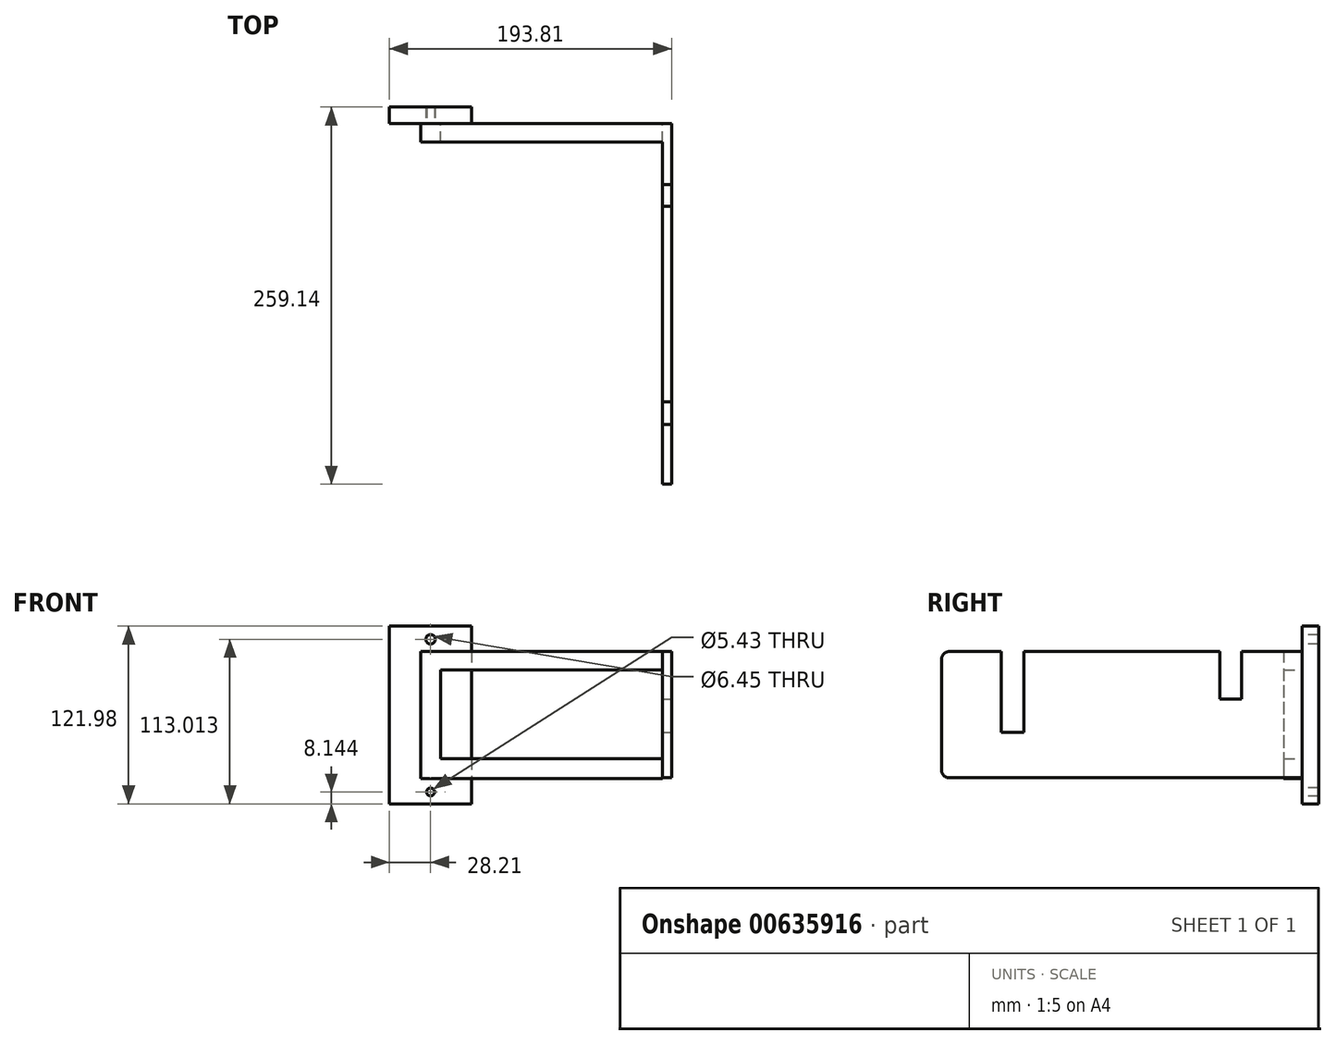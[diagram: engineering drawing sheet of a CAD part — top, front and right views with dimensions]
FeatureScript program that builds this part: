
annotation { "Feature Type Name" : "Feature", "Feature Type Description" : "" }
export const myFeature = defineFeature(function(context is Context, id is Id, definition is map)
    precondition{}
    {
        {
            var Q0;
            Q0=qCreatedBy(makeId("Front.planeOp"),FACE);
            var sketch = newSketch(context, id + "F0", { "sketchPlane" : qUnion([Q0])});
            skLineSegment(sketch, "E0.bottom", {"start": v(28.21, 61) * mm, "end": v(-28.21, 61) * mm});
            skLineSegment(sketch, "E0.top", {"start": v(28.21, -61) * mm, "end": v(-28.21, -61) * mm});
            skLineSegment(sketch, "E0.left", {"start": v(28.21, 61) * mm, "end": v(28.21, -61) * mm});
            skLineSegment(sketch, "E0.right", {"start": v(-28.21, 61) * mm, "end": v(-28.21, -61) * mm});
            skPoint(sketch, "E0.middle", {"position": v(0, 0) * mm});
            skSolve(sketch);
        }
        {
            var Q0;
            Q0=makeQuery(id+"F0.imprint","IMPRINT",FACE,{"disambiguationData":[TD([[makeQuery(id+"F0.imprint","IMPRINT",EDGE,{"derivedFrom":sQuery(id+"F0.wireOp",EDGE,"E0.bottom")}),1.0]])]});
            extrude(context, id + "F1", {"entities" : qUnion([Q0]), "depth" : 6.35 * mm, "offsetDistance" : 25.4 * mm});
        }
        {
            var Q0;
            Q0=makeQuery(id+"F1.opExtrude","CAP_FACE",FACE,{"disambiguationData":[OSD([sQuery(id+"F0.wireOp",EDGE,"E0.bottom"),sQuery(id+"F0.wireOp",EDGE,"E0.top"),sQuery(id+"F0.wireOp",EDGE,"E0.left"),sQuery(id+"F0.wireOp",EDGE,"E0.right")])],"isStart":false});
            var sketch = newSketch(context, id + "F2", { "sketchPlane" : qUnion([Q0])});
            skLineSegment(sketch, "E1.bottom", {"start": v(6.85, 43.57) * mm, "end": v(-6.85, 43.57) * mm});
            skLineSegment(sketch, "E1.top", {"start": v(6.85, -43.57) * mm, "end": v(-6.85, -43.57) * mm});
            skLineSegment(sketch, "E1.left", {"start": v(6.85, 43.57) * mm, "end": v(6.85, -43.57) * mm});
            skLineSegment(sketch, "E1.right", {"start": v(-6.85, 43.57) * mm, "end": v(-6.85, -43.57) * mm});
            skPoint(sketch, "E1.middle", {"position": v(0, 0) * mm});
            skSolve(sketch);
        }
        {
            var Q0;
            Q0 = qSketchRegion(id + "F2", true);
            extrude(context, id + "F3", {"entities" : qUnion([Q0]), "operationType" : NewBodyOperationType.ADD, "depth" : 12.7 * mm, "offsetDistance" : 25.4 * mm});
        }
        {
            var Q0;
            Q0=makeQuery(id+"F3.opExtrude","SWEPT_FACE",FACE,{"disambiguationData":[OSD([sQuery(id+"F2.wireOp",EDGE,"E1.left")])]});
            var sketch = newSketch(context, id + "F4", { "sketchPlane" : qUnion([Q0])});
            skLineSegment(sketch, "E2.bottom", {"start": v(-19.05, 43.57) * mm, "end": v(-6.35, 43.57) * mm});
            skLineSegment(sketch, "E2.top", {"start": v(-19.05, 30.9) * mm, "end": v(-6.35, 30.9) * mm});
            skLineSegment(sketch, "E2.left", {"start": v(-19.05, 43.57) * mm, "end": v(-19.05, 30.9) * mm});
            skLineSegment(sketch, "E2.right", {"start": v(-6.35, 43.57) * mm, "end": v(-6.35, 30.9) * mm});
            skSolve(sketch);
        }
        {
            var Q0;
            Q0 = qSketchRegion(id + "F4", true);
            extrude(context, id + "F5", {"entities" : qUnion([Q0]), "operationType" : NewBodyOperationType.ADD, "depth" : 152.4 * mm, "offsetDistance" : 25.4 * mm});
        }
        {
            var Q0;
            Q0=makeQuery(id+"F3.opExtrude","SWEPT_FACE",FACE,{"disambiguationData":[OSD([sQuery(id+"F2.wireOp",EDGE,"E1.left")])]});
            var sketch = newSketch(context, id + "F6", { "sketchPlane" : qUnion([Q0])});
            skLineSegment(sketch, "E3.bottom", {"start": v(-19.05, -43.57) * mm, "end": v(-6.35, -43.57) * mm});
            skLineSegment(sketch, "E3.top", {"start": v(-19.05, -30.1) * mm, "end": v(-6.35, -30.1) * mm});
            skLineSegment(sketch, "E3.left", {"start": v(-19.05, -43.57) * mm, "end": v(-19.05, -30.1) * mm});
            skLineSegment(sketch, "E3.right", {"start": v(-6.35, -43.57) * mm, "end": v(-6.35, -30.1) * mm});
            skSolve(sketch);
        }
        {
            var Q0;
            Q0 = qSketchRegion(id + "F6", true);
            extrude(context, id + "F7", {"entities" : qUnion([Q0]), "operationType" : NewBodyOperationType.ADD, "depth" : 152.4 * mm, "offsetDistance" : 25.4 * mm});
        }
        {
            var Q0;
            {var subQ0=sQuery(id+"F0.wireOp",EDGE,"E0.left");var subQ1=sQuery(id+"F0.wireOp",EDGE,"E0.bottom");var subQ2=sQuery(id+"F0.wireOp",EDGE,"E0.right");var subQ3=sQuery(id+"F0.wireOp",EDGE,"E0.top");Q0=makeQuery(id+"F7.boolean.opBoolean","SPLIT",FACE,{"disambiguationData":[TD([makeQuery(id+"F1.opExtrude","SWEPT_FACE",FACE,{"disambiguationData":[OSD([subQ1])]})])],"derivedFrom":makeQuery(id+"F1.opExtrude","CAP_FACE",FACE,{"disambiguationData":[OSD([subQ1,subQ3,subQ0,subQ2])],"isStart":false})});}
            var sketch = newSketch(context, id + "F8", { "sketchPlane" : qUnion([Q0])});
            skCircle(sketch, "E4", {"center": v(0, 52.02) * mm, "radius": 3.22 * mm});
            skPoint(sketch, "E4.centerSnap0", {"position": v(0, 61) * mm});
            skCircle(sketch, "E5", {"center": v(0, -52.85) * mm, "radius": 2.71 * mm});
            skPoint(sketch, "E5.centerSnap0", {"position": v(0, -61) * mm});
            skSolve(sketch);
        }
        {
            var Q0;
            Q0 = qSketchRegion(id + "F8", true);
            extrude(context, id + "F9", {"entities" : qUnion([Q0]), "operationType" : NewBodyOperationType.REMOVE, "endBound" : BoundingType.THROUGH_ALL, "oppositeDirection" : true, "depth" : 25.4 * mm, "offsetDistance" : 25.4 * mm});
        }
        {
            var Q0;
            Q0=makeQuery(id+"F5.opExtrude","CAP_FACE",FACE,{"disambiguationData":[OSD([sQuery(id+"F4.wireOp",EDGE,"E2.bottom"),sQuery(id+"F4.wireOp",EDGE,"E2.top"),sQuery(id+"F4.wireOp",EDGE,"E2.left"),sQuery(id+"F4.wireOp",EDGE,"E2.right")])],"isStart":false});
            var sketch = newSketch(context, id + "F10", { "sketchPlane" : qUnion([Q0])});
            skLineSegment(sketch, "E6.bottom", {"start": v(-6.35, 43.57) * mm, "end": v(-254.06, 43.57) * mm});
            skLineSegment(sketch, "E6.top", {"start": v(-6.35, -43.1) * mm, "end": v(-254.06, -43.1) * mm});
            skLineSegment(sketch, "E6.left", {"start": v(-6.35, 43.57) * mm, "end": v(-6.35, -43.1) * mm});
            skLineSegment(sketch, "E6.right", {"start": v(-254.06, 43.57) * mm, "end": v(-254.06, -43.1) * mm});
            skSolve(sketch);
        }
        {
            var Q0;
            Q0 = qSketchRegion(id + "F10", true);
            extrude(context, id + "F11", {"entities" : qUnion([Q0]), "operationType" : NewBodyOperationType.ADD, "depth" : 6.35 * mm, "offsetDistance" : 25.4 * mm});
        }
        {
            var Q0;
            Q0=makeQuery(id+"F11.opExtrude","CAP_FACE",FACE,{"disambiguationData":[OSD([sQuery(id+"F10.wireOp",EDGE,"E6.bottom"),sQuery(id+"F10.wireOp",EDGE,"E6.top"),sQuery(id+"F10.wireOp",EDGE,"E6.left"),sQuery(id+"F10.wireOp",EDGE,"E6.right")])],"isStart":false});
            var sketch = newSketch(context, id + "F12", { "sketchPlane" : qUnion([Q0])});
            skLineSegment(sketch, "E7.bottom", {"start": v(-48.14, 55.23) * mm, "end": v(-63.02, 55.23) * mm});
            skLineSegment(sketch, "E7.top", {"start": v(-48.14, 10.88) * mm, "end": v(-63.02, 10.88) * mm});
            skLineSegment(sketch, "E7.left", {"start": v(-48.14, 55.23) * mm, "end": v(-48.14, 10.88) * mm});
            skLineSegment(sketch, "E7.right", {"start": v(-63.02, 55.23) * mm, "end": v(-63.02, 10.88) * mm});
            skLineSegment(sketch, "E8.bottom", {"start": v(-197.53, 66.58) * mm, "end": v(-213.1, 66.58) * mm});
            skLineSegment(sketch, "E8.top", {"start": v(-197.53, -11.88) * mm, "end": v(-213.1, -11.88) * mm});
            skLineSegment(sketch, "E8.left", {"start": v(-197.53, 66.58) * mm, "end": v(-197.53, -11.88) * mm});
            skLineSegment(sketch, "E8.right", {"start": v(-213.1, 66.58) * mm, "end": v(-213.1, -11.88) * mm});
            skSolve(sketch);
        }
        {
            var Q0;
            Q0 = qSketchRegion(id + "F12", true);
            extrude(context, id + "F13", {"entities" : qUnion([Q0]), "operationType" : NewBodyOperationType.REMOVE, "oppositeDirection" : true, "depth" : 25.4 * mm, "offsetDistance" : 25.4 * mm});
        }
        {
            var Q0;
            Q0=makeQuery(id+"F11.opExtrude","SWEPT_EDGE",EDGE,{"disambiguationData":[OSD([sQuery(id+"F10.wireOp",EDGE,"E6.bottom"),sQuery(id+"F10.wireOp",EDGE,"E6.right")])]});
            var Q1;
            Q1=makeQuery(id+"F11.opExtrude","SWEPT_EDGE",EDGE,{"disambiguationData":[OSD([sQuery(id+"F10.wireOp",EDGE,"E6.top"),sQuery(id+"F10.wireOp",EDGE,"E6.right")])]});
            fillet(context, id + "F14", {"entities" : qUnion([Q0, Q1]), "radius" : 5.08 * mm, "tangentPropagation" : true, "allowEdgeOverflow" : false});
        }
        {
            var Q0;
            Q0=makeQuery(id+"F1.opExtrude","CAP_FACE",FACE,{"disambiguationData":[OSD([sQuery(id+"F0.wireOp",EDGE,"E0.bottom"),sQuery(id+"F0.wireOp",EDGE,"E0.top"),sQuery(id+"F0.wireOp",EDGE,"E0.left"),sQuery(id+"F0.wireOp",EDGE,"E0.right")])],"isStart":true});
            extrude(context, id + "F15", {"entities" : qUnion([Q0]), "operationType" : NewBodyOperationType.ADD, "depth" : 5.08 * mm, "offsetDistance" : 25.4 * mm});
        }
        {
            var Q0;
            {var subQ0=sQuery(id+"F0.wireOp",EDGE,"E0.left");Q0=makeQuery(id+"F7.boolean.opBoolean","SPLIT",FACE,{"disambiguationData":[TD([makeQuery(id+"F3.opExtrude","SWEPT_FACE",FACE,{"disambiguationData":[OSD([sQuery(id+"F2.wireOp",EDGE,"E1.left")])]})])],"derivedFrom":makeQuery(id+"F1.opExtrude","CAP_FACE",FACE,{"disambiguationData":[OSD([sQuery(id+"F0.wireOp",EDGE,"E0.bottom"),sQuery(id+"F0.wireOp",EDGE,"E0.top"),subQ0,sQuery(id+"F0.wireOp",EDGE,"E0.right")])],"isStart":false})});}
            var sketch = newSketch(context, id + "F16", { "sketchPlane" : qUnion([Q0])});
            skCircle(sketch, "E9", {"center": v(17.64, 0) * mm, "radius": 4.39 * mm});
            skSolve(sketch);
        }
        {
            var Q0;
            Q0=sQuery(id+"F16.wireOp",EDGE,"E9");
            extrude(context, id + "F17", {"bodyType" : ToolBodyType.SURFACE, "surfaceEntities" : qUnion([Q0]), "endBound" : BoundingType.THROUGH_ALL, "depth" : 25.4 * mm, "offsetDistance" : 25.4 * mm});
        }
    });
